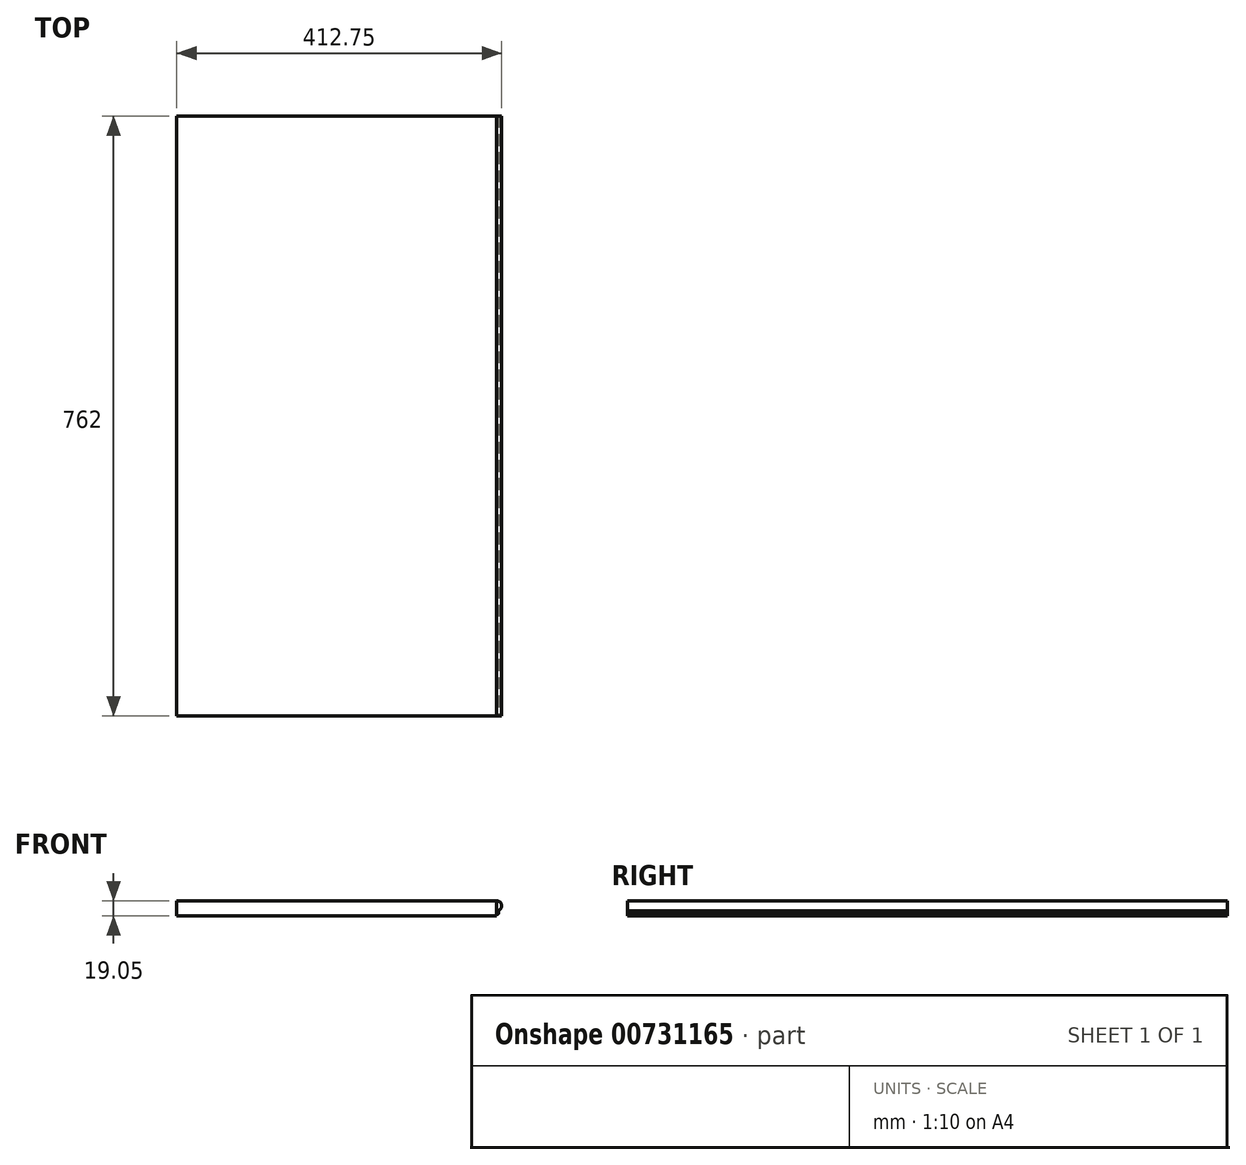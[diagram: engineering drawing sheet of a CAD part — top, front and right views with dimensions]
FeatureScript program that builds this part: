
annotation { "Feature Type Name" : "Feature", "Feature Type Description" : "" }
export const myFeature = defineFeature(function(context is Context, id is Id, definition is map)
    precondition{}
    {
        {
            var Q0;
            Q0=qCreatedBy(makeId("Top.planeOp"),FACE);
            var sketch = newSketch(context, id + "F0", { "sketchPlane" : qUnion([Q0])});
            skLineSegment(sketch, "E0.bottom", {"start": v(203.2, 381) * mm, "end": v(-203.2, 381) * mm});
            skLineSegment(sketch, "E0.top", {"start": v(203.2, -381) * mm, "end": v(-203.2, -381) * mm});
            skLineSegment(sketch, "E0.left", {"start": v(203.2, 381) * mm, "end": v(203.2, -381) * mm});
            skLineSegment(sketch, "E0.right", {"start": v(-203.2, 381) * mm, "end": v(-203.2, -381) * mm});
            skPoint(sketch, "E0.middle", {"position": v(0, 0) * mm});
            skSolve(sketch);
        }
        {
            var Q0;
            Q0 = qSketchRegion(id + "F0", true);
            extrude(context, id + "F1", {"entities" : qUnion([Q0]), "depth" : 19.05 * mm, "offsetDistance" : 25.4 * mm});
        }
        {
            var Q0;
            Q0=makeQuery(id+"F1.opExtrude","SWEPT_FACE",FACE,{"disambiguationData":[OSD([sQuery(id+"F0.wireOp",EDGE,"E0.top")])]});
            var sketch = newSketch(context, id + "F2", { "sketchPlane" : qUnion([Q0])});
            skArc(sketch, "E1", {"start": v(204.72, 6.54) * mm, "mid": v(209.5, 13.47) * mm, "end": v(203.2, 19.05) * mm});
            skArc(sketch, "E2", {"start": v(204.72, 1.78) * mm, "mid": v(205.74, 3.81) * mm, "end": v(204.72, 5.84) * mm});
            skLineSegment(sketch, "E3", {"start": v(204.72, 6.54) * mm, "end": v(204.72, 1.78) * mm});
            skLineSegment(sketch, "E4", {"start": v(203.2, 19.05) * mm, "end": v(203.2, 0.97) * mm});
            skLineSegment(sketch, "E5", {"start": v(204.72, 1.78) * mm, "end": v(203.2, 1.78) * mm});
            skSolve(sketch);
        }
        {
            var Q0;
            {var subQ1=sQuery(id+"F2.wireOp",EDGE,"E1");Q0=makeQuery(id+"F2.imprint","IMPRINT",FACE,{"disambiguationData":[TD([[makeQuery(id+"F2.imprint","IMPRINT",EDGE,{"derivedFrom":subQ1}),1.0]])]});}
            var Q1;
            {var subQ0=sQuery(id+"F2.wireOp",EDGE,"E2");Q1=makeQuery(id+"F2.imprint","IMPRINT",FACE,{"disambiguationData":[TD([[makeQuery(id+"F2.imprint","IMPRINT",EDGE,{"derivedFrom":subQ0}),1.0]])]});}
            var Q2;
            Q2=makeQuery(id+"F1.opExtrude","SWEPT_FACE",FACE,{"disambiguationData":[OSD([sQuery(id+"F0.wireOp",EDGE,"E0.bottom")])]});
            extrude(context, id + "F3", {"entities" : qUnion([Q0, Q1]), "endBound" : BoundingType.UP_TO_SURFACE, "oppositeDirection" : true, "depth" : 25.4 * mm, "endBoundEntityFace" : qUnion([Q2]), "offsetDistance" : 25.4 * mm});
        }
    });
